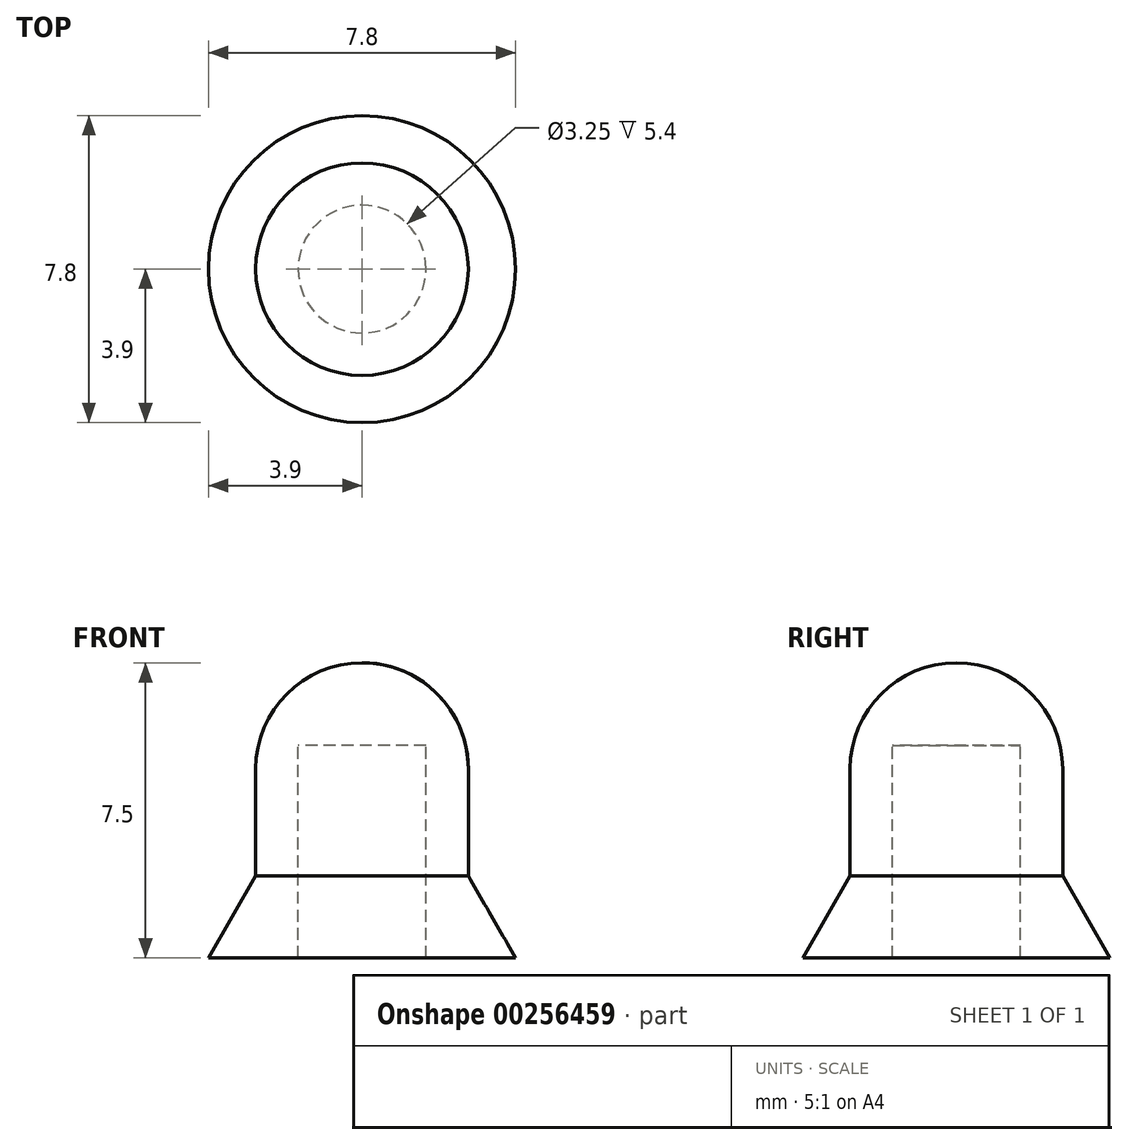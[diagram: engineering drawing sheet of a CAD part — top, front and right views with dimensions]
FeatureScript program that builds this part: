
annotation { "Feature Type Name" : "Feature", "Feature Type Description" : "" }
export const myFeature = defineFeature(function(context is Context, id is Id, definition is map)
    precondition{}
    {
        {
            var Q0;
            Q0=qCreatedBy(makeId("Front.planeOp"),FACE);
            var sketch = newSketch(context, id + "F0", { "sketchPlane" : qUnion([Q0])});
            skLineSegment(sketch, "E0", {"start": v(0.54, 0) * mm, "end": v(1.3, 0) * mm});
            skLineSegment(sketch, "E1", {"start": v(1.3, 0) * mm, "end": v(0.9, 0.7) * mm});
            skLineSegment(sketch, "E2", {"start": v(0.9, 0.7) * mm, "end": v(0.9, 1.6) * mm});
            skArc(sketch, "E3", {"start": v(0.9, 1.6) * mm, "mid": v(0.64, 2.24) * mm, "end": v(0, 2.5) * mm});
            skLineSegment(sketch, "E4", {"start": v(0, 1.8) * mm, "end": v(0.54, 1.8) * mm});
            skLineSegment(sketch, "E5", {"start": v(0.54, 1.8) * mm, "end": v(0.54, 0) * mm});
            skLineSegment(sketch, "E6", {"start": v(0, 2.5) * mm, "end": v(0, 1.8) * mm});
            skSolve(sketch);
        }
        {
            var Q0;
            Q0=makeQuery(id+"F0.imprint","IMPRINT",FACE,{"disambiguationData":[TD([[makeQuery(id+"F0.imprint","IMPRINT",EDGE,{"derivedFrom":sQuery(id+"F0.wireOp",EDGE,"E0")}),1.0]])]});
            var Q1;
            Q1=sQuery(id+"F0.wireOp",EDGE,"E6");
            revolve(context, id + "F1", {"entities" : qUnion([Q0]), "axis" : qUnion([Q1]), "revolveType" : RevolveType.FULL});
        }
        {
            var Q0;
            Q0=makeQuery(id+"F1.opRevolve","SWEPT_BODY",BODY,{"disambiguationData":[OSD([sQuery(id+"F0.wireOp",EDGE,"E0"),sQuery(id+"F0.wireOp",EDGE,"E1"),sQuery(id+"F0.wireOp",EDGE,"E2"),sQuery(id+"F0.wireOp",EDGE,"E3"),sQuery(id+"F0.wireOp",EDGE,"E4"),sQuery(id+"F0.wireOp",EDGE,"E5"),sQuery(id+"F0.wireOp",EDGE,"E6")])]});
            var Q1;
            Q1=qCreatedBy(makeId("Origin.pointOp"),VERTEX);
            transform(context, id + "F2", {"entities" : qUnion([Q0]), "transformType" : TransformType.SCALE_UNIFORMLY, "scale" : 3, "makeCopy" : false, "scalePoint" : qUnion([Q1])});
        }
    });
